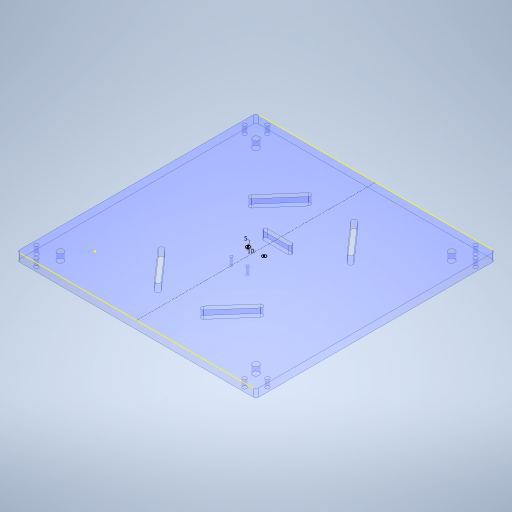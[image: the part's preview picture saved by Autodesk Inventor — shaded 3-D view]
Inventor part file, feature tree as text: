
AUTODESK INVENTOR PART (.ipt)
format: ipt  version: 2023 (Build 270158000, 158)  size: 422,912 bytes
history: native  units: mm
features: sketch x11, extrude x10, plane x1, mirror x1, fillet x1, other x1
ambient origin geometry x8: Origin, YZ Plane, XZ Plane, XY Plane, X Axis, Y Axis, Z Axis, Center Point
bodies: Solid1 (feature_tree)
feature tree (25):
  extrude  "Extrusion1"  Depth=8.1mm
  extrude  "Extrusion2"  Depth=8.1mm
  extrude  "Extrusion3"  Depth=6.0mm
  plane  "Work Plane1"
  mirror  "Mirror1"
  extrude  "Extrusion4"  Depth=55.0mm
  extrude  "Extrusion5"  Depth=55.0mm
  extrude  "Extrusion6"  Depth=6.0mm
  extrude  "Extrusion8"  Depth=6.0mm
  extrude  "Extrusion7"  Depth=50.0mm
  extrude  "Extrusion9"  Depth=10.0mm TaperAngle=0.0deg
  extrude  "Extrusion10"  Depth=5.0mm
  fillet  "Fillet1"  Radius=100.0mm
  sketch  "Sketch13"  dims[d25=10.0mm d26=0.0mm d27=21.105mm d28=8.1mm d29=10.0mm d30=10.0mm d31=0.0mm d32=20.0mm d33=3.0mm d34=3.0mm d36=10.0mm d37=0.0mm d38=10.0mm d39=0.0mm d40=10.0mm d41=19.0mm d42=25.0mm d43=5.0mm d44=35.0mm d45=10.0mm d46=0.0mm d47=10.0mm d48=0.0mm d49=2.0mm d50=10.0mm d51=5.0mm]
  sketch  "Sketch1"  dims[d0=8.1mm d1=8.1mm]
  sketch  "Sketch2"  dims[d2=8.1mm d3=8.1mm]
  sketch  "Sketch3"  dims[d4=10.0mm d5=0.0mm d6=6.0mm]
  sketch  "Sketch4"  dims[d7=120.0mm d8=55.0mm]
  sketch  "Sketch5"  dims[d9=120.0mm d10=55.0mm]
  sketch  "Sketch7"  dims[d11=6.0mm d12=148.5mm]
  sketch  "Sketch9"  dims[d13=10.0mm d14=0.0mm d15=6.0mm]
  sketch  "Sketch10"  dims[d16=8.5mm d17=50.0mm]
  sketch  "Sketch11"  dims[d18=10.0mm d19=0.0mm d20=10.0mm d21=0.0mm]
  sketch  "Sketch12"  dims[d22=10.0mm d23=5.0mm d24=100.0mm]
  other  "Cut-Extrude14"
